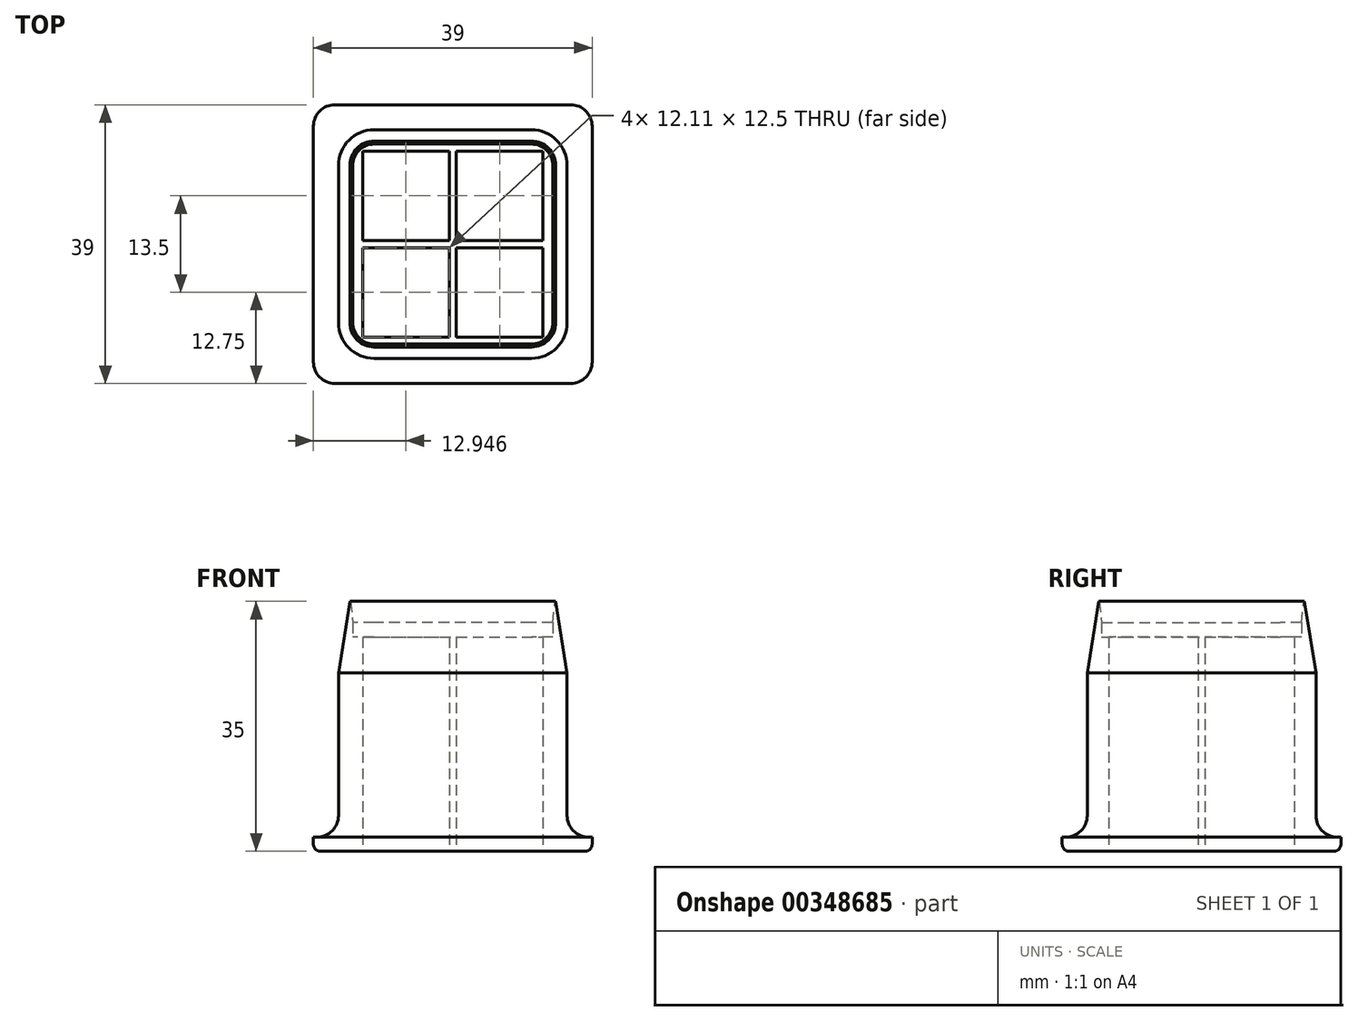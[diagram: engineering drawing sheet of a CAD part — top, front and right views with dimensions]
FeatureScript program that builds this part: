
annotation { "Feature Type Name" : "Feature", "Feature Type Description" : "" }
export const myFeature = defineFeature(function(context is Context, id is Id, definition is map)
    precondition{}
    {
        {
            var Q0;
            Q0=qCreatedBy(makeId("Top.planeOp"),FACE);
            var sketch = newSketch(context, id + "F0", { "sketchPlane" : qUnion([Q0])});
            skLineSegment(sketch, "E0", {"start": v(-14, 11) * mm, "end": v(-14, -11) * mm});
            skLineSegment(sketch, "E1", {"start": v(14, -11) * mm, "end": v(14, 11) * mm});
            skLineSegment(sketch, "E2", {"start": v(-11, 14) * mm, "end": v(11, 14) * mm});
            skLineSegment(sketch, "E3", {"start": v(-11, -14) * mm, "end": v(11, -14) * mm});
            skLineSegment(sketch, "E4", {"start": v(0, 14) * mm, "end": v(0, -14) * mm, "construction": true});
            skLineSegment(sketch, "E5", {"start": v(-14, 0) * mm, "end": v(14, 0) * mm, "construction": true});
            skPoint(sketch, "E6", {"position": v(0, 0) * mm});
            skPoint(sketch, "E7", {"position": v(0, 14) * mm});
            skPoint(sketch, "E8", {"position": v(0, -14) * mm});
            skPoint(sketch, "E9", {"position": v(-14, 0) * mm});
            skPoint(sketch, "E10", {"position": v(14, 0) * mm});
            skArc(sketch, "E11", {"start": v(-11, 14) * mm, "mid": v(-13.12, 13.12) * mm, "end": v(-14, 11) * mm});
            skArc(sketch, "E12", {"start": v(14, 11) * mm, "mid": v(13.12, 13.12) * mm, "end": v(11, 14) * mm});
            skArc(sketch, "E13", {"start": v(-14, -11) * mm, "mid": v(-13.12, -13.12) * mm, "end": v(-11, -14) * mm});
            skArc(sketch, "E14", {"start": v(11, -14) * mm, "mid": v(13.12, -13.12) * mm, "end": v(14, -11) * mm});
            skLineSegment(sketch, "E15.bottom", {"start": v(-19.5, 19.5) * mm, "end": v(19.5, 19.5) * mm});
            skLineSegment(sketch, "E15.top", {"start": v(-19.5, -19.5) * mm, "end": v(19.5, -19.5) * mm});
            skLineSegment(sketch, "E15.left", {"start": v(-19.5, 19.5) * mm, "end": v(-19.5, -19.5) * mm});
            skLineSegment(sketch, "E15.right", {"start": v(19.5, 19.5) * mm, "end": v(19.5, -19.5) * mm});
            skLineSegment(sketch, "E16", {"start": v(-16, 11) * mm, "end": v(-16, -11) * mm});
            skLineSegment(sketch, "E17", {"start": v(-11, 16) * mm, "end": v(11, 16) * mm});
            skLineSegment(sketch, "E18", {"start": v(16, 11) * mm, "end": v(16, -11) * mm});
            skLineSegment(sketch, "E19", {"start": v(11, -16) * mm, "end": v(-11, -16) * mm});
            skArc(sketch, "E20", {"start": v(-11, 16) * mm, "mid": v(-14.54, 14.54) * mm, "end": v(-16, 11) * mm});
            skArc(sketch, "E21", {"start": v(16, 11) * mm, "mid": v(14.54, 14.54) * mm, "end": v(11, 16) * mm});
            skArc(sketch, "E22", {"start": v(11, -16) * mm, "mid": v(14.54, -14.54) * mm, "end": v(16, -11) * mm});
            skArc(sketch, "E23", {"start": v(-16, -11) * mm, "mid": v(-14.54, -14.54) * mm, "end": v(-11, -16) * mm});
            skLineSegment(sketch, "E24.bottom", {"start": v(-12.6, 13) * mm, "end": v(12.6, 13) * mm});
            skLineSegment(sketch, "E24.top", {"start": v(-12.6, -13) * mm, "end": v(12.6, -13) * mm});
            skLineSegment(sketch, "E24.left", {"start": v(-12.6, 13) * mm, "end": v(-12.6, -13) * mm});
            skLineSegment(sketch, "E24.right", {"start": v(12.6, 13) * mm, "end": v(12.6, -13) * mm});
            skLineSegment(sketch, "E25.bottom", {"start": v(-12.6, -0.5) * mm, "end": v(12.6, -0.5) * mm});
            skLineSegment(sketch, "E25.top", {"start": v(-12.6, 0.5) * mm, "end": v(12.6, 0.5) * mm});
            skLineSegment(sketch, "E25.left", {"start": v(-12.6, -0.5) * mm, "end": v(-12.6, 0.5) * mm});
            skLineSegment(sketch, "E25.right", {"start": v(12.6, -0.5) * mm, "end": v(12.6, 0.5) * mm});
            skLineSegment(sketch, "E26.bottom", {"start": v(0.5, 13) * mm, "end": v(-0.5, 13) * mm});
            skLineSegment(sketch, "E26.top", {"start": v(0.5, -13) * mm, "end": v(-0.5, -13) * mm});
            skLineSegment(sketch, "E26.left", {"start": v(0.5, 13) * mm, "end": v(0.5, -13) * mm});
            skLineSegment(sketch, "E26.right", {"start": v(-0.5, 13) * mm, "end": v(-0.5, -13) * mm});
            skSolve(sketch);
        }
        {
            var Q0;
            Q0=makeQuery(id+"F0.imprint","IMPRINT",FACE,{"disambiguationData":[TD([[makeQuery(id+"F0.imprint","IMPRINT",EDGE,{"derivedFrom":sQuery(id+"F0.wireOp",EDGE,"E15.bottom")}),-1.0]])]});
            var Q1;
            Q1=makeQuery(id+"F0.imprint","IMPRINT",FACE,{"disambiguationData":[TD([[makeQuery(id+"F0.imprint","IMPRINT",EDGE,{"derivedFrom":sQuery(id+"F0.wireOp",EDGE,"E0")}),-1.0]])]});
            extrude(context, id + "F1", {"entities" : qUnion([Q0, Q1]), "depth" : 2 * mm});
        }
        {
            var Q0;
            Q0=makeQuery(id+"F0.imprint","IMPRINT",FACE,{"disambiguationData":[TD([[makeQuery(id+"F0.imprint","IMPRINT",EDGE,{"derivedFrom":sQuery(id+"F0.wireOp",EDGE,"E0")}),-1.0]])]});
            extrude(context, id + "F2", {"entities" : qUnion([Q0]), "operationType" : NewBodyOperationType.ADD, "depth" : 35 * mm});
        }
        {
            var Q0;
            Q0=makeQuery(id+"F2.opExtrude","CAP_EDGE",EDGE,{"disambiguationData":[OSD([sQuery(id+"F0.wireOp",EDGE,"E19")])],"isStart":false});
            var Q1;
            Q1=makeQuery(id+"F2.opExtrude","CAP_EDGE",EDGE,{"disambiguationData":[OSD([sQuery(id+"F0.wireOp",EDGE,"E22")])],"isStart":false});
            var Q2;
            Q2=makeQuery(id+"F2.opExtrude","CAP_EDGE",EDGE,{"disambiguationData":[OSD([sQuery(id+"F0.wireOp",EDGE,"E18")])],"isStart":false});
            var Q3;
            Q3=makeQuery(id+"F2.opExtrude","CAP_EDGE",EDGE,{"disambiguationData":[OSD([sQuery(id+"F0.wireOp",EDGE,"E21")])],"isStart":false});
            var Q4;
            Q4=makeQuery(id+"F2.opExtrude","CAP_EDGE",EDGE,{"disambiguationData":[OSD([sQuery(id+"F0.wireOp",EDGE,"E17")])],"isStart":false});
            var Q5;
            Q5=makeQuery(id+"F2.opExtrude","CAP_EDGE",EDGE,{"disambiguationData":[OSD([sQuery(id+"F0.wireOp",EDGE,"E20")])],"isStart":false});
            var Q6;
            Q6=makeQuery(id+"F2.opExtrude","CAP_EDGE",EDGE,{"disambiguationData":[OSD([sQuery(id+"F0.wireOp",EDGE,"E16")])],"isStart":false});
            var Q7;
            Q7=makeQuery(id+"F2.opExtrude","CAP_EDGE",EDGE,{"disambiguationData":[OSD([sQuery(id+"F0.wireOp",EDGE,"E23")])],"isStart":false});
            chamfer(context, id + "F3", {"entities" : qUnion([Q0, Q1, Q2, Q3, Q4, Q5, Q6, Q7]), "chamferType" : ChamferType.TWO_OFFSETS, "width1" : 10 * mm, "oppositeDirection" : false, "width2" : 1.6 * mm, "tangentPropagation" : true});
        }
        {
            var Q0;
            Q0=makeQuery(id+"F0.imprint","IMPRINT",FACE,{"disambiguationData":[TD([[makeQuery(id+"F0.imprint","IMPRINT",EDGE,{"derivedFrom":sQuery(id+"F0.wireOp",EDGE,"E0")}),1.0]])]});
            extrude(context, id + "F4", {"entities" : qUnion([Q0]), "operationType" : NewBodyOperationType.ADD, "depth" : 30 * mm});
        }
        {
            var Q0;
            Q0=makeQuery(id+"F2.opExtrude","CAP_EDGE",EDGE,{"disambiguationData":[OSD([sQuery(id+"F0.wireOp",EDGE,"E2")])],"isStart":false});
            var Q1;
            Q1=makeQuery(id+"F2.opExtrude","CAP_EDGE",EDGE,{"disambiguationData":[OSD([sQuery(id+"F0.wireOp",EDGE,"E12")])],"isStart":false});
            var Q2;
            Q2=makeQuery(id+"F2.opExtrude","CAP_EDGE",EDGE,{"disambiguationData":[OSD([sQuery(id+"F0.wireOp",EDGE,"E1")])],"isStart":false});
            var Q3;
            Q3=makeQuery(id+"F2.opExtrude","CAP_EDGE",EDGE,{"disambiguationData":[OSD([sQuery(id+"F0.wireOp",EDGE,"E14")])],"isStart":false});
            var Q4;
            Q4=makeQuery(id+"F2.opExtrude","CAP_EDGE",EDGE,{"disambiguationData":[OSD([sQuery(id+"F0.wireOp",EDGE,"E3")])],"isStart":false});
            var Q5;
            Q5=makeQuery(id+"F2.opExtrude","CAP_EDGE",EDGE,{"disambiguationData":[OSD([sQuery(id+"F0.wireOp",EDGE,"E13")])],"isStart":false});
            var Q6;
            Q6=makeQuery(id+"F2.opExtrude","CAP_EDGE",EDGE,{"disambiguationData":[OSD([sQuery(id+"F0.wireOp",EDGE,"E0")])],"isStart":false});
            var Q7;
            Q7=makeQuery(id+"F2.opExtrude","CAP_EDGE",EDGE,{"disambiguationData":[OSD([sQuery(id+"F0.wireOp",EDGE,"E11")])],"isStart":false});
            chamfer(context, id + "F5", {"entities" : qUnion([Q0, Q1, Q2, Q3, Q4, Q5, Q6, Q7]), "chamferType" : ChamferType.TWO_OFFSETS, "width1" : 0.3 * mm, "oppositeDirection" : false, "width2" : 3 * mm, "tangentPropagation" : true});
        }
        {
            var Q0;
            {var subQ0=sQuery(id+"F0.wireOp",EDGE,"E25.bottom");var subQ1=sQuery(id+"F0.wireOp",EDGE,"E24.right");var subQ2=makeQuery(id+"F0.imprint","INTERSECT",VERTEX,{"derivedFrom":[subQ1,subQ0]});Q0=makeQuery(id+"F0.imprint","IMPRINT",FACE,{"disambiguationData":[TD([[makeQuery(id+"F0.imprint","IMPRINT",EDGE,{"disambiguationData":[TD([[subQ2,1.0]])],"derivedFrom":subQ1}),-1.0]])]});}
            var Q1;
            {var subQ0=sQuery(id+"F0.wireOp",EDGE,"E26.left");var subQ1=sQuery(id+"F0.wireOp",EDGE,"E24.top");var subQ2=makeQuery(id+"F0.imprint","INTERSECT",VERTEX,{"derivedFrom":[subQ1,subQ0]});Q1=makeQuery(id+"F0.imprint","IMPRINT",FACE,{"disambiguationData":[TD([[makeQuery(id+"F0.imprint","IMPRINT",EDGE,{"disambiguationData":[TD([[subQ2,1.0]])],"derivedFrom":subQ1}),1.0]])]});}
            var Q2;
            {var subQ0=sQuery(id+"F0.wireOp",EDGE,"E25.bottom");var subQ1=sQuery(id+"F0.wireOp",EDGE,"E24.left");var subQ2=makeQuery(id+"F0.imprint","INTERSECT",VERTEX,{"derivedFrom":[subQ1,subQ0]});Q2=makeQuery(id+"F0.imprint","IMPRINT",FACE,{"disambiguationData":[TD([[makeQuery(id+"F0.imprint","IMPRINT",EDGE,{"disambiguationData":[TD([[subQ2,1.0]])],"derivedFrom":subQ1}),1.0]])]});}
            var Q3;
            {var subQ0=sQuery(id+"F0.wireOp",EDGE,"E26.left");var subQ1=sQuery(id+"F0.wireOp",EDGE,"E25.bottom");var subQ2=makeQuery(id+"F0.imprint","INTERSECT",VERTEX,{"derivedFrom":[subQ1,subQ0]});Q3=makeQuery(id+"F0.imprint","IMPRINT",FACE,{"disambiguationData":[TD([[makeQuery(id+"F0.imprint","IMPRINT",EDGE,{"disambiguationData":[TD([[subQ2,1.0]])],"derivedFrom":subQ1}),1.0]])]});}
            var Q4;
            {var subQ0=sQuery(id+"F0.wireOp",EDGE,"E26.left");var subQ1=sQuery(id+"F0.wireOp",EDGE,"E24.bottom");var subQ2=makeQuery(id+"F0.imprint","INTERSECT",VERTEX,{"derivedFrom":[subQ1,subQ0]});Q4=makeQuery(id+"F0.imprint","IMPRINT",FACE,{"disambiguationData":[TD([[makeQuery(id+"F0.imprint","IMPRINT",EDGE,{"disambiguationData":[TD([[subQ2,1.0]])],"derivedFrom":subQ1}),-1.0]])]});}
            extrude(context, id + "F6", {"entities" : qUnion([Q0, Q1, Q2, Q3, Q4]), "operationType" : NewBodyOperationType.ADD, "depth" : 30 * mm});
        }
        {
            var Q0;
            Q0=makeQuery(id+"F2.boolean.opBoolean","INTERSECT",EDGE,{"derivedFrom":[makeQuery(id+"F1.opExtrude","CAP_FACE",FACE,{"disambiguationData":[OSD([sQuery(id+"F0.wireOp",EDGE,"E0"),sQuery(id+"F0.wireOp",EDGE,"E1"),sQuery(id+"F0.wireOp",EDGE,"E2"),sQuery(id+"F0.wireOp",EDGE,"E3"),sQuery(id+"F0.wireOp",EDGE,"E11"),sQuery(id+"F0.wireOp",EDGE,"E12"),sQuery(id+"F0.wireOp",EDGE,"E13"),sQuery(id+"F0.wireOp",EDGE,"E14"),sQuery(id+"F0.wireOp",EDGE,"E15.bottom"),sQuery(id+"F0.wireOp",EDGE,"E15.top"),sQuery(id+"F0.wireOp",EDGE,"E15.left"),sQuery(id+"F0.wireOp",EDGE,"E15.right")])],"isStart":false}),makeQuery(id+"F2.opExtrude","SWEPT_FACE",FACE,{"disambiguationData":[OSD([sQuery(id+"F0.wireOp",EDGE,"E17")])]})]});
            var Q1;
            Q1=makeQuery(id+"F1.opExtrude","SWEPT_EDGE",EDGE,{"disambiguationData":[OSD([sQuery(id+"F0.wireOp",EDGE,"E15.bottom"),sQuery(id+"F0.wireOp",EDGE,"E15.left")])]});
            var Q2;
            Q2=makeQuery(id+"F1.opExtrude","SWEPT_EDGE",EDGE,{"disambiguationData":[OSD([sQuery(id+"F0.wireOp",EDGE,"E15.bottom"),sQuery(id+"F0.wireOp",EDGE,"E15.right")])]});
            var Q3;
            Q3=makeQuery(id+"F1.opExtrude","SWEPT_EDGE",EDGE,{"disambiguationData":[OSD([sQuery(id+"F0.wireOp",EDGE,"E15.top"),sQuery(id+"F0.wireOp",EDGE,"E15.left")])]});
            var Q4;
            Q4=makeQuery(id+"F1.opExtrude","SWEPT_EDGE",EDGE,{"disambiguationData":[OSD([sQuery(id+"F0.wireOp",EDGE,"E15.top"),sQuery(id+"F0.wireOp",EDGE,"E15.right")])]});
            fillet(context, id + "F7", {"entities" : qUnion([Q0, Q1, Q2, Q3, Q4]), "radius" : 3 * mm, "tangentPropagation" : true, "allowEdgeOverflow" : false});
        }
        {
            var Q0;
            Q0=makeQuery(id+"F1.opExtrude","CAP_EDGE",EDGE,{"disambiguationData":[OSD([sQuery(id+"F0.wireOp",EDGE,"E15.top")])],"isStart":true});
            fillet(context, id + "F8", {"entities" : qUnion([Q0]), "radius" : 1 * mm, "tangentPropagation" : true, "allowEdgeOverflow" : false});
        }
    });
